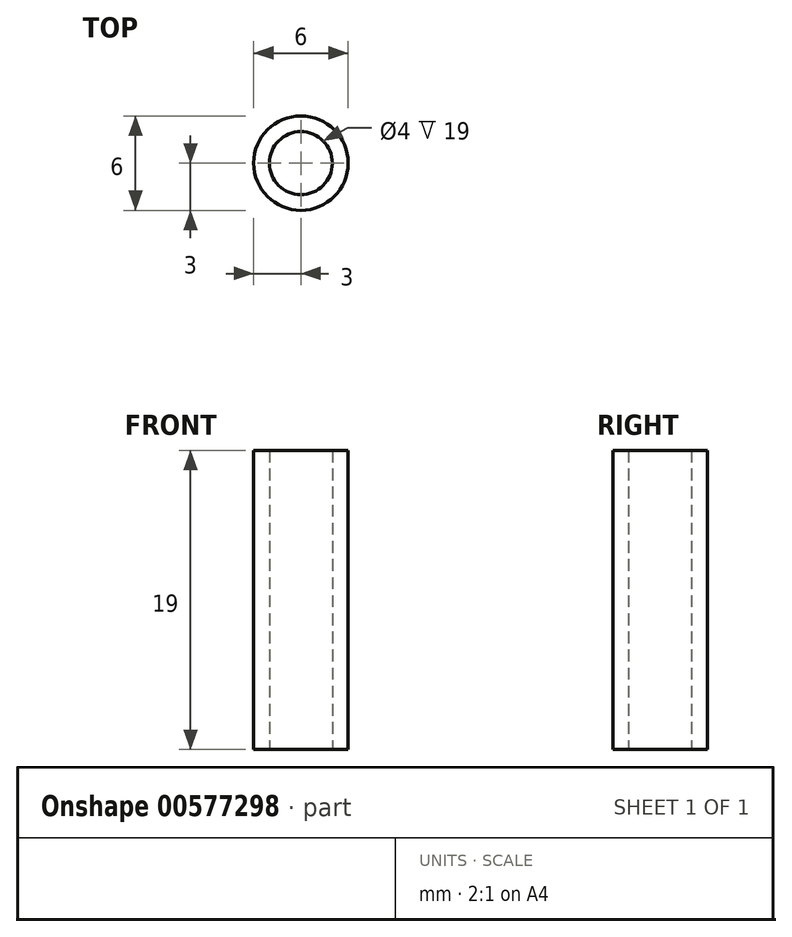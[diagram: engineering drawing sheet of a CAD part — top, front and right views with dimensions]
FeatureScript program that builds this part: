
annotation { "Feature Type Name" : "Feature", "Feature Type Description" : "" }
export const myFeature = defineFeature(function(context is Context, id is Id, definition is map)
    precondition{}
    {
        {
            var Q0;
            Q0=qCreatedBy(makeId("Top.planeOp"),FACE);
            var sketch = newSketch(context, id + "F0", { "sketchPlane" : qUnion([Q0])});
            skCircle(sketch, "E0", {"center": v(0, 0) * mm, "radius": 2 * mm});
            skCircle(sketch, "E1", {"center": v(0, 0) * mm, "radius": 3 * mm});
            skSolve(sketch);
        }
        {
            var Q0;
            Q0 = qSketchRegion(id + "F0", true);
            extrude(context, id + "F1", {"entities" : qUnion([Q0]), "depth" : 19 * mm, "offsetDistance" : 25 * mm});
        }
    });
